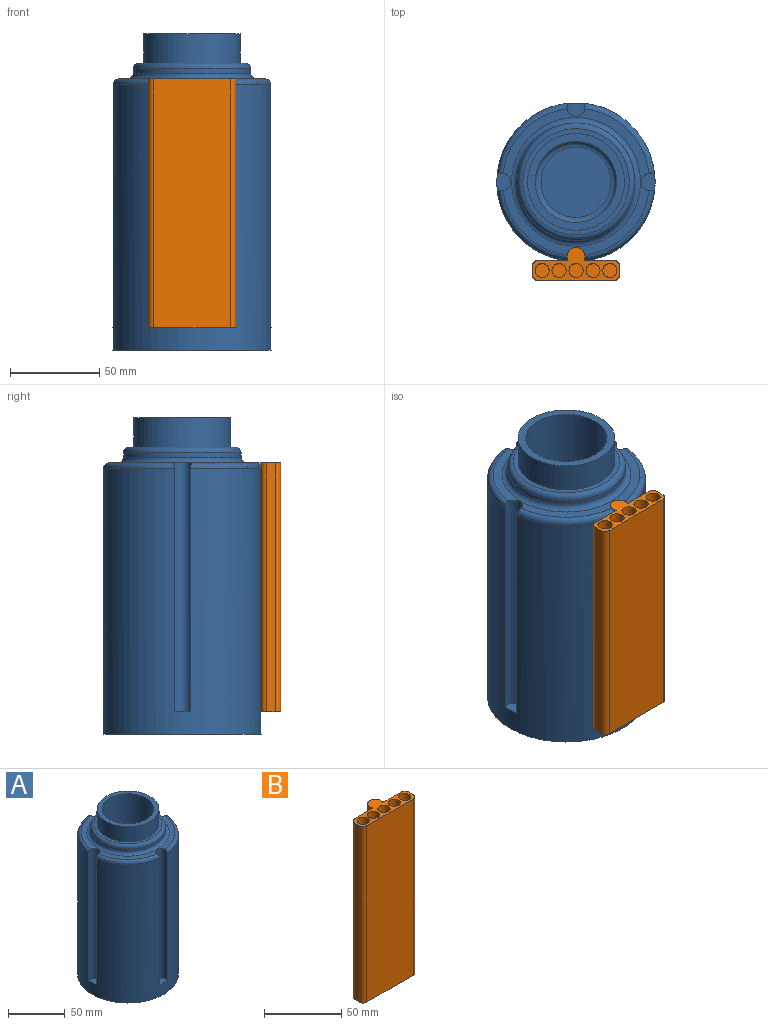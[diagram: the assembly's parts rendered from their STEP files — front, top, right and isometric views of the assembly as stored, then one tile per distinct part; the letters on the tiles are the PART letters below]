
ASSEMBLY  parts=2 mates=1
PART A: 24 faces, bbox 95.7x95.7x177.8 mm
  f0: cylinder r=44.45mm len=149.23mm, axis (0,0,-1), area 36726mm2, adj f2,f3,f4,f5,f6,f7,f8,f9
  f1: plane 81.94x81.94mm, normal (0,0,1), area 1104mm2, adj f3,f5,f7,f9,f15,f19,f20,f21
  f2: plane 88.9x88.9mm, normal (0,0,-1), area 6207.2mm2, adj f0
  f3: cylinder r=5.08mm len=139.7mm, axis (0,0,1), area 2894.5mm2, adj f0,f1,f4,f19,f20
  f4: plane 10.16x7.62mm, normal (0,0,1), area 64.6mm2, adj f0,f3
  f5: cylinder r=5.08mm len=139.7mm, axis (0,0,1), area 2894.5mm2, adj f0,f1,f6,f19,f22
  f6: plane 10.16x7.62mm, normal (0,0,1), area 64.6mm2, adj f0,f5
  f7: cylinder r=5.08mm len=139.7mm, axis (0,0,1), area 2894.5mm2, adj f0,f1,f8,f21,f22
  f8: plane 10.16x7.62mm, normal (0,0,1), area 64.6mm2, adj f0,f7
  f9: cylinder r=5.08mm len=139.7mm, axis (0,0,1), area 2894.5mm2, adj f0,f1,f10,f20,f21
  f10: plane 10.16x7.62mm, normal (0,0,1), area 64.6mm2, adj f0,f9
  f11: cylinder r=33.02mm len=66.04mm, axis (0,0,1), area 527mm2, adj f15,f16
  f12: plane 59.69x59.69mm, normal (0,0,1), area 477.8mm2, adj f13,f16
  f13: cylinder r=27.18mm len=54.36mm, axis (0,0,1), area 2819.3mm2, adj f12,f14
  f14: plane 54.36x54.36mm, normal (0,0,1), area 678.8mm2, adj f13,f17
  f15: torus R=36.2mm, axis (0,0,1), area 1070.9mm2, adj f1,f11
  f16: torus R=29.84mm, axis (0,0,-1), area 998.6mm2, adj f11,f12
  f17: cylinder r=22.86mm len=161.93mm, axis (0,0,1), area 23257.9mm2, adj f14,f23
  f18: plane 39.37x39.37mm, normal (0,0,1), area 1217.4mm2, adj f23
  f19: torus R=41.27mm, axis (0,0,1), area 290.7mm2, adj f0,f1,f3,f5
  f20: torus R=41.27mm, axis (0,0,1), area 290.7mm2, adj f0,f1,f3,f9
  f21: torus R=41.27mm, axis (0,0,1), area 290.7mm2, adj f0,f1,f7,f9
  f22: torus R=41.27mm, axis (0,0,1), area 290.7mm2, adj f0,f1,f5,f7
  f23: torus R=19.69mm, axis (0,0,1), area 680.2mm2, adj f17,f18
PART B: 22 faces, bbox 49.2x18.5x139.7 mm
  f0: plane 139.7x16.91mm, normal (0,1,0), area 2361.8mm2, adj f10,f11,f12,f18
  f1: plane 139.7x4.76mm, normal (-1,0,0), area 665.3mm2, adj f11,f12,f18,f19
  f2: plane 139.7x42.86mm, normal (0,-1,0), area 5987.9mm2, adj f11,f12,f19,f20
  f3: plane 139.7x4.76mm, normal (1,0,0), area 665.3mm2, adj f11,f12,f20,f21
  f4: plane 139.7x16.91mm, normal (0,1,0), area 2361.8mm2, adj f10,f11,f12,f21
  f5: cylinder r=3.97mm len=114.3mm, axis (0,0,-1), area 2850.2mm2, adj f11,f13
  f6: cylinder r=3.97mm len=114.3mm, axis (0,0,-1), area 2850.2mm2, adj f11,f14
  f7: cylinder r=3.97mm len=114.3mm, axis (0,0,-1), area 2850.2mm2, adj f11,f15
  f8: cylinder r=3.97mm len=114.3mm, axis (0,0,-1), area 2850.2mm2, adj f11,f16
  f9: cylinder r=3.97mm len=114.3mm, axis (0,0,-1), area 2850.2mm2, adj f11,f17
  f10: cylinder r=5.08mm len=139.7mm, axis (0,0,-1), area 2899.3mm2, adj f0,f4,f11,f12
  f11: plane 49.21x18.5mm, normal (0,0,1), area 354mm2, adj f0,f1,f2,f3,f4,f5,f6,f7
  f12: plane 49.21x18.5mm, normal (0,0,-1), area 601.4mm2, adj f0,f1,f2,f3,f4,f10,f18,f19
  f13: plane 7.94x7.94mm, normal (0,0,1), area 49.5mm2, adj f5
  f14: plane 7.94x7.94mm, normal (0,0,1), area 49.5mm2, adj f6
  f15: plane 7.94x7.94mm, normal (0,0,1), area 49.5mm2, adj f7
  f16: plane 7.94x7.94mm, normal (0,0,1), area 49.5mm2, adj f8
  f17: plane 7.94x7.94mm, normal (0,0,1), area 49.5mm2, adj f9
  f18: cylinder r=3.17mm len=139.7mm, axis (0,0,1), area 696.7mm2, adj f0,f1,f11,f12
  f19: cylinder r=3.17mm len=139.7mm, axis (0,0,-1), area 696.7mm2, adj f1,f2,f11,f12
  f20: cylinder r=3.17mm len=139.7mm, axis (0,0,1), area 696.7mm2, adj f2,f3,f11,f12
  f21: cylinder r=3.17mm len=139.7mm, axis (0,0,-1), area 696.7mm2, adj f3,f4,f11,f12
PLACE A t=(-88.65,8.93,-7.44)mm fixed
PLACE B t=(-88.65,8.93,5.26)mm
MATE slider B.f10 <-> A.f5  axis (0,0,-1) through (-88.65,-32.98,75.11)mm
